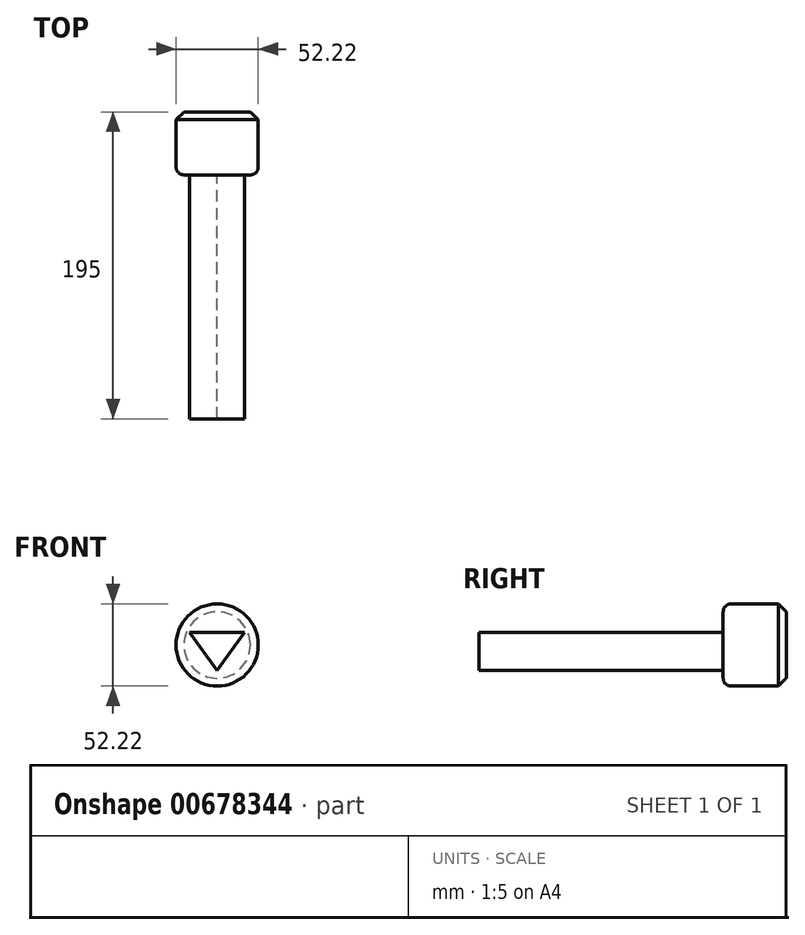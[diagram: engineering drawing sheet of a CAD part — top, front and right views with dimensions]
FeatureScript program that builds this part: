
annotation { "Feature Type Name" : "Feature", "Feature Type Description" : "" }
export const myFeature = defineFeature(function(context is Context, id is Id, definition is map)
    precondition{}
    {
        {
            var Q0;
            Q0=qCreatedBy(makeId("Front.planeOp"),FACE);
            var sketch = newSketch(context, id + "F0", { "sketchPlane" : qUnion([Q0])});
            skLineSegment(sketch, "E0", {"start": v(-17.5, 8.12) * mm, "end": v(17.5, 8.12) * mm});
            skLineSegment(sketch, "E1", {"start": v(17.5, 8.12) * mm, "end": v(0, -16.24) * mm});
            skLineSegment(sketch, "E2", {"start": v(0, -16.24) * mm, "end": v(-17.5, 8.12) * mm});
            skSolve(sketch);
        }
        {
            var Q0;
            Q0=makeQuery(id+"F0.imprint","IMPRINT",FACE,{"disambiguationData":[TD([[makeQuery(id+"F0.imprint","IMPRINT",EDGE,{"derivedFrom":sQuery(id+"F0.wireOp",EDGE,"E0")}),-1.0]])]});
            extrude(context, id + "F1", {"entities" : qUnion([Q0]), "depth" : 155 * mm, "offsetDistance" : 25 * mm});
        }
        {
            var Q0;
            Q0=qCreatedBy(makeId("Front.planeOp"),FACE);
            var sketch = newSketch(context, id + "F2", { "sketchPlane" : qUnion([Q0])});
            skCircle(sketch, "E3", {"center": v(0, 0) * mm, "radius": 26.1 * mm});
            skSolve(sketch);
        }
        {
            var Q0;
            Q0=makeQuery(id+"F2.imprint","IMPRINT",FACE,{"disambiguationData":[TD([[makeQuery(id+"F2.imprint","IMPRINT",EDGE,{"derivedFrom":sQuery(id+"F2.wireOp",EDGE,"E3")}),1.0]])]});
            extrude(context, id + "F3", {"entities" : qUnion([Q0]), "operationType" : NewBodyOperationType.ADD, "oppositeDirection" : true, "depth" : 40 * mm, "offsetDistance" : 25 * mm});
        }
        {
            var Q0;
            Q0=makeQuery(id+"F3.opExtrude","CAP_EDGE",EDGE,{"disambiguationData":[OSD([sQuery(id+"F2.wireOp",EDGE,"E3")])],"isStart":false});
            chamfer(context, id + "F4", {"entities" : qUnion([Q0]), "width" : 5 * mm, "tangentPropagation" : true});
        }
        {
            var Q0;
            Q0=makeQuery(id+"F3.opExtrude","CAP_EDGE",EDGE,{"disambiguationData":[OSD([sQuery(id+"F2.wireOp",EDGE,"E3")])],"isStart":true});
            fillet(context, id + "F5", {"entities" : qUnion([Q0]), "radius" : 5 * mm, "tangentPropagation" : true, "allowEdgeOverflow" : false});
        }
    });
